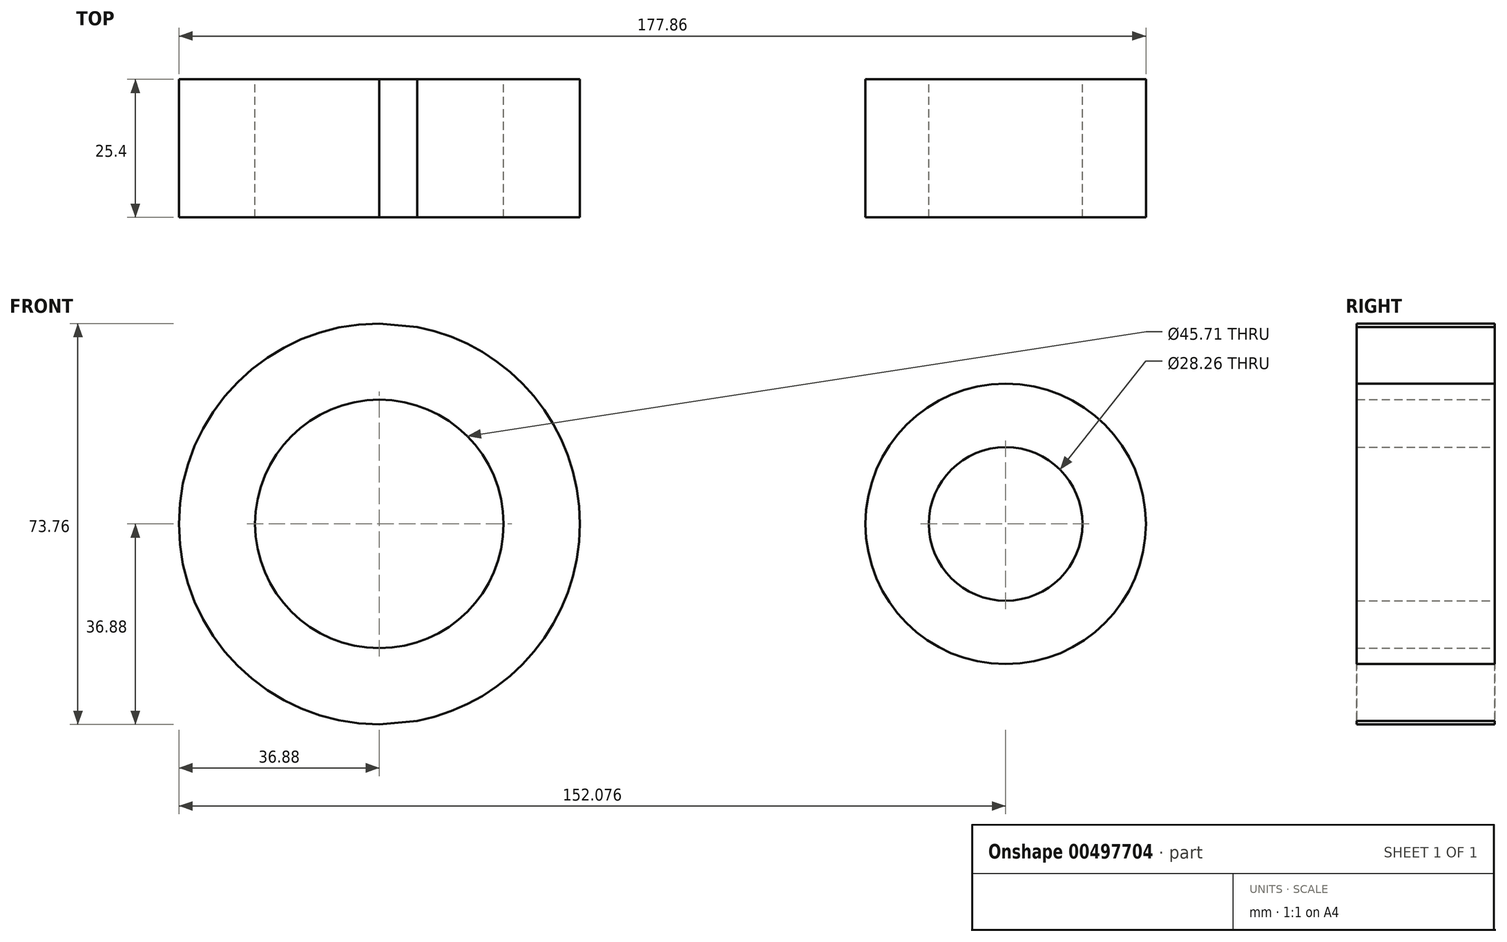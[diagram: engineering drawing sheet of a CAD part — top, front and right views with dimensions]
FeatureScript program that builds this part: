
annotation { "Feature Type Name" : "Feature", "Feature Type Description" : "" }
export const myFeature = defineFeature(function(context is Context, id is Id, definition is map)
    precondition{}
    {
        {
            var Q0;
            Q0=qCreatedBy(makeId("Front.planeOp"),FACE);
            var sketch = newSketch(context, id + "F0", { "sketchPlane" : qUnion([Q0])});
            skCircle(sketch, "E0", {"center": v(0, 0) * mm, "radius": 36.88 * mm});
            skCircle(sketch, "E1", {"center": v(115.2, 0) * mm, "radius": 25.79 * mm});
            skCircle(sketch, "E2", {"center": v(115.2, 0) * mm, "radius": 14.13 * mm});
            skCircle(sketch, "E3", {"center": v(0, 0) * mm, "radius": 22.85 * mm});
            skLineSegment(sketch, "E4", {"start": v(0, 36.88) * mm, "end": v(117.64, 25.67) * mm});
            skLineSegment(sketch, "E5", {"start": v(0, -36.88) * mm, "end": v(117.64, -25.67) * mm});
            skSolve(sketch);
        }
        {
            var Q0;
            Q0=makeQuery(id+"F0.imprint","IMPRINT",FACE,{"disambiguationData":[TD([[makeQuery(id+"F0.imprint","IMPRINT",EDGE,{"derivedFrom":sQuery(id+"F0.wireOp",EDGE,"E3")}),-1.0]])]});
            var Q1;
            {var subQ0=sQuery(id+"F0.wireOp",EDGE,"E4");var subQ1=sQuery(id+"F0.wireOp",EDGE,"E0");var subQ2=makeQuery(id+"F0.imprint","INTERSECT",VERTEX,{"disambiguationData":[OD(1.0)],"derivedFrom":[subQ1,subQ0]});Q1=makeQuery(id+"F0.imprint","IMPRINT",FACE,{"disambiguationData":[TD([[makeQuery(id+"F0.imprint","IMPRINT",EDGE,{"disambiguationData":[TD([[subQ2,1.0]])],"derivedFrom":subQ1}),-1.0]])]});}
            var Q2;
            Q2=makeQuery(id+"F0.imprint","IMPRINT",FACE,{"disambiguationData":[TD([[makeQuery(id+"F0.imprint","IMPRINT",EDGE,{"derivedFrom":sQuery(id+"F0.wireOp",EDGE,"E2")}),-1.0]])]});
            extrude(context, id + "F1", {"entities" : qUnion([Q0, Q1, Q2]), "depth" : 25.4 * mm});
        }
    });
